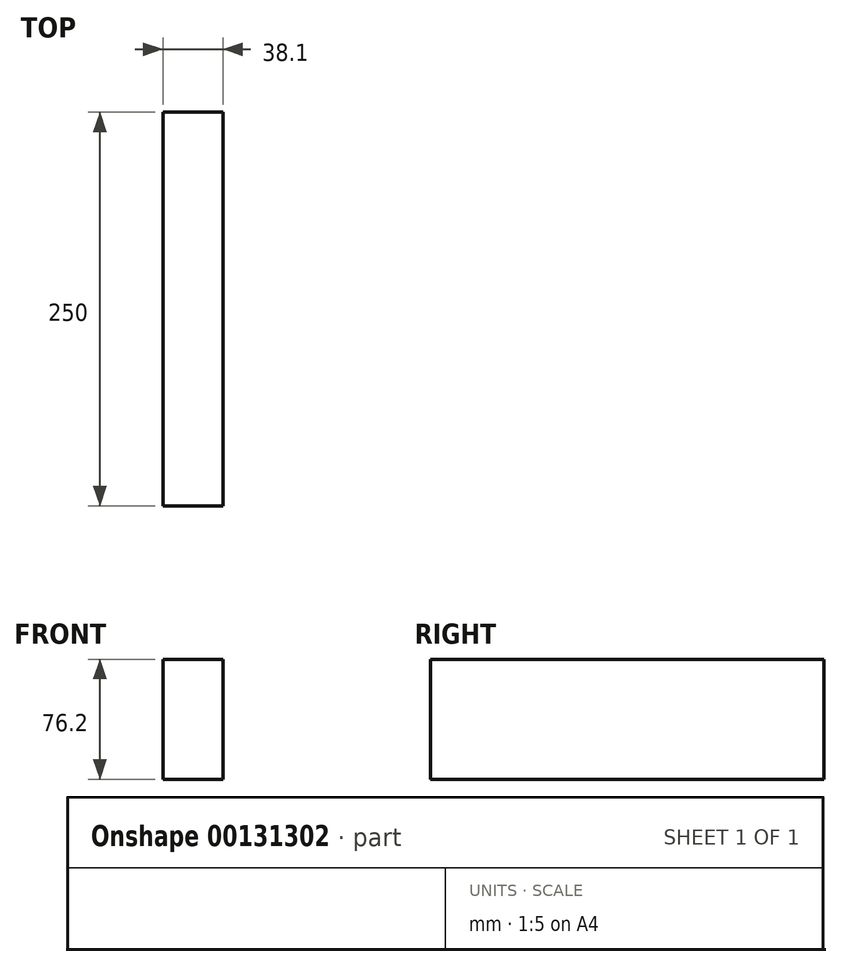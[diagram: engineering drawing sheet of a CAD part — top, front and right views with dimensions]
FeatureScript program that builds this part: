
annotation { "Feature Type Name" : "Feature", "Feature Type Description" : "" }
export const myFeature = defineFeature(function(context is Context, id is Id, definition is map)
    precondition{}
    {
        {
            var Q0;
            Q0=qCreatedBy(makeId("Front.planeOp"),FACE);
            var sketch = newSketch(context, id + "F0", { "sketchPlane" : qUnion([Q0])});
            skLineSegment(sketch, "E0", {"start": v(-55.37, 51.95) * mm, "end": v(-55.37, -24.25) * mm});
            skLineSegment(sketch, "E1", {"start": v(-55.37, -24.25) * mm, "end": v(-17.27, -24.25) * mm});
            skLineSegment(sketch, "E2", {"start": v(-17.27, -24.25) * mm, "end": v(-17.27, 51.95) * mm});
            skLineSegment(sketch, "E3", {"start": v(-17.27, 51.95) * mm, "end": v(-55.37, 51.95) * mm});
            skSolve(sketch);
        }
        {
            var Q0;
            Q0=makeQuery(id+"F0.imprint","IMPRINT",FACE,{"disambiguationData":[TD([[makeQuery(id+"F0.imprint","IMPRINT",EDGE,{"derivedFrom":sQuery(id+"F0.wireOp",EDGE,"E0")}),1.0]])]});
            extrude(context, id + "F1", {"entities" : qUnion([Q0]), "depth" : 250 * mm});
        }
    });
